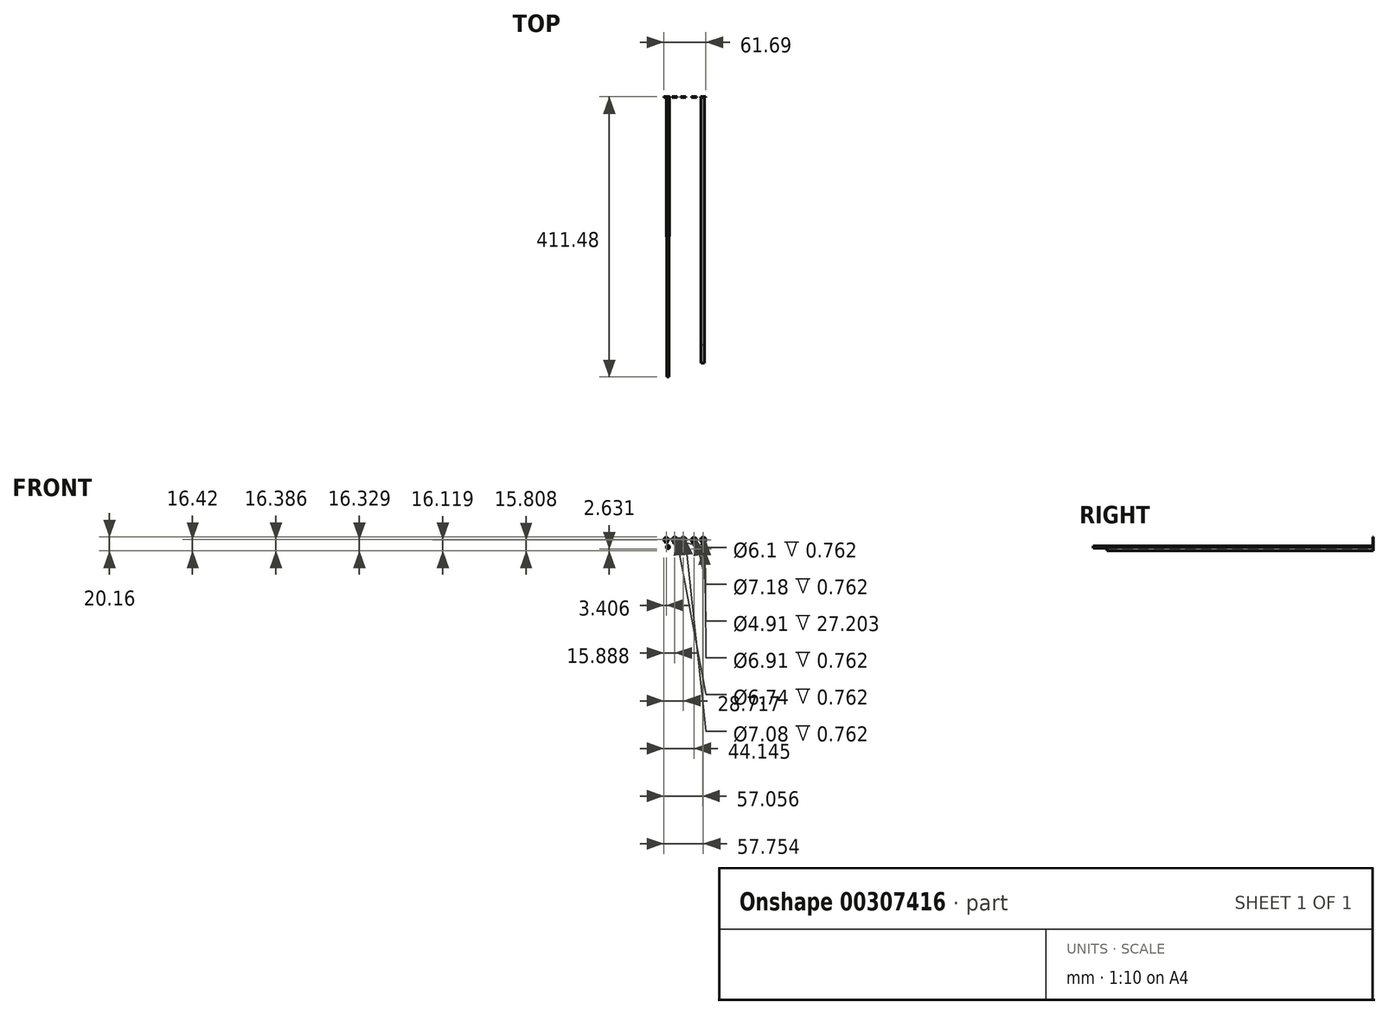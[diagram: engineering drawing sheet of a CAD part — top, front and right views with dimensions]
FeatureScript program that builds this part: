
annotation { "Feature Type Name" : "Feature", "Feature Type Description" : "" }
export const myFeature = defineFeature(function(context is Context, id is Id, definition is map)
    precondition{}
    {
        {
            var Q0;
            Q0=qCreatedBy(makeId("Front.planeOp"),FACE);
            var sketch = newSketch(context, id + "F0", { "sketchPlane" : qUnion([Q0])});
            skCircle(sketch, "E0", {"center": v(33.39, 22.16) * mm, "radius": 2.63 * mm});
            skSolve(sketch);
        }
        {
            var Q0;
            Q0=makeQuery(id+"F0.imprint","IMPRINT",FACE,{"disambiguationData":[TD([[makeQuery(id+"F0.imprint","IMPRINT",EDGE,{"derivedFrom":sQuery(id+"F0.wireOp",EDGE,"E0")}),1.0]])]});
            extrude(context, id + "F1", {"entities" : qUnion([Q0]), "depth" : 391.16 * mm});
        }
        {
            var Q0;
            Q0=makeQuery(id+"F1.opExtrude","CAP_FACE",FACE,{"disambiguationData":[OSD([sQuery(id+"F0.wireOp",EDGE,"E0")])],"isStart":false});
            var sketch = newSketch(context, id + "F2", { "sketchPlane" : qUnion([Q0])});
            skCircle(sketch, "E1", {"center": v(33.39, 22.16) * mm, "radius": 2.45 * mm});
            skSolve(sketch);
        }
        {
            var Q0;
            Q0 = qSketchRegion(id + "F2", true);
            extrude(context, id + "F3", {"entities" : qUnion([Q0]), "operationType" : NewBodyOperationType.REMOVE, "oppositeDirection" : true, "depth" : 27.2 * mm});
        }
        {
            var Q0;
            Q0=qCreatedBy(makeId("Front.planeOp"),FACE);
            var sketch = newSketch(context, id + "F4", { "sketchPlane" : qUnion([Q0])});
            skCircle(sketch, "E2", {"center": v(-17.76, 24.97) * mm, "radius": 2.45 * mm});
            skSolve(sketch);
        }
        {
            var Q0;
            Q0=makeQuery(id+"F4.imprint","IMPRINT",FACE,{"disambiguationData":[TD([[makeQuery(id+"F4.imprint","IMPRINT",EDGE,{"derivedFrom":sQuery(id+"F4.wireOp",EDGE,"E2")}),1.0]])]});
            extrude(context, id + "F5", {"entities" : qUnion([Q0]), "depth" : 411.48 * mm, "hasDraft" : true, "draftAngle" : 0.1 * degree, "draftPullDirection" : true});
        }
        {
            var Q0;
            Q0=qCreatedBy(makeId("Front.planeOp"),FACE);
            var sketch = newSketch(context, id + "F6", { "sketchPlane" : qUnion([Q0])});
            skCircle(sketch, "E3", {"center": v(34.08, 35.65) * mm, "radius": 3.93 * mm});
            skCircle(sketch, "E4", {"center": v(34.08, 35.65) * mm, "radius": 3.46 * mm});
            skLineSegment(sketch, "E5", {"start": v(34.31, 31.72) * mm, "end": v(34.31, 28.21) * mm});
            skLineSegment(sketch, "E6", {"start": v(33.85, 31.72) * mm, "end": v(33.85, 28.21) * mm});
            skLineSegment(sketch, "E7", {"start": v(33.85, 28.21) * mm, "end": v(34.31, 28.21) * mm});
            skLineSegment(sketch, "E8", {"start": v(35.77, 32.1) * mm, "end": v(36.19, 28.21) * mm});
            skLineSegment(sketch, "E9", {"start": v(36.19, 28.21) * mm, "end": v(35.55, 28.21) * mm});
            skLineSegment(sketch, "E10", {"start": v(35.55, 28.21) * mm, "end": v(35.3, 31.91) * mm});
            skLineSegment(sketch, "E11", {"start": v(32.4, 32.1) * mm, "end": v(32.14, 28.21) * mm});
            skLineSegment(sketch, "E12", {"start": v(32.14, 28.21) * mm, "end": v(32.68, 28.18) * mm});
            skLineSegment(sketch, "E13", {"start": v(32.68, 28.18) * mm, "end": v(32.92, 31.91) * mm});
            skSolve(sketch);
        }
        {
            var Q0;
            Q0=makeQuery(id+"F6.imprint","IMPRINT",FACE,{"disambiguationData":[TD([[makeQuery(id+"F6.imprint","IMPRINT",EDGE,{"derivedFrom":sQuery(id+"F6.wireOp",EDGE,"E4")}),-1.0]])]});
            var Q1;
            {var subQ0=sQuery(id+"F6.wireOp",EDGE,"AtMkA9jw-oHao-wLgf-iVHr-EhoPNY91XVLY");Q1=makeQuery(id+"F6.imprint","IMPRINT",FACE,{"disambiguationData":[TD([[makeQuery(id+"F6.imprint","IMPRINT",EDGE,{"derivedFrom":subQ0}),-1.0]])]});}
            var Q2;
            {var subQ0=sQuery(id+"F6.wireOp",EDGE,"G1UfZidr-wi69-PWyG-ggrf-osr7YpHfYW1K");Q2=makeQuery(id+"F6.imprint","IMPRINT",FACE,{"disambiguationData":[TD([[makeQuery(id+"F6.imprint","IMPRINT",EDGE,{"derivedFrom":subQ0}),1.0]])]});}
            var Q3;
            {var subQ0=sQuery(id+"F6.wireOp",EDGE,"wkRRPSaf-uJ6Z-lWe9-TKJw-fEsDiBzZJhiO");Q3=makeQuery(id+"F6.imprint","IMPRINT",FACE,{"disambiguationData":[TD([[makeQuery(id+"F6.imprint","IMPRINT",EDGE,{"derivedFrom":subQ0}),1.0]])]});}
            extrude(context, id + "F7", {"entities" : qUnion([Q0, Q1, Q2, Q3]), "depth" : 0.76 * mm});
        }
        {
            var Q0;
            Q0=makeQuery(id+"F6.imprint","IMPRINT",FACE,{"disambiguationData":[TD([[makeQuery(id+"F6.imprint","IMPRINT",EDGE,{"derivedFrom":sQuery(id+"F6.wireOp",EDGE,"E4")}),-1.0]])]});
            var Q1;
            {var subQ0=sQuery(id+"F6.wireOp",EDGE,"E11");Q1=makeQuery(id+"F6.imprint","IMPRINT",FACE,{"disambiguationData":[TD([[makeQuery(id+"F6.imprint","IMPRINT",EDGE,{"derivedFrom":subQ0}),1.0]])]});}
            var Q2;
            {var subQ0=sQuery(id+"F6.wireOp",EDGE,"E5");Q2=makeQuery(id+"F6.imprint","IMPRINT",FACE,{"disambiguationData":[TD([[makeQuery(id+"F6.imprint","IMPRINT",EDGE,{"derivedFrom":subQ0}),-1.0]])]});}
            var Q3;
            {var subQ0=sQuery(id+"F6.wireOp",EDGE,"E8");Q3=makeQuery(id+"F6.imprint","IMPRINT",FACE,{"disambiguationData":[TD([[makeQuery(id+"F6.imprint","IMPRINT",EDGE,{"derivedFrom":subQ0}),-1.0]])]});}
            extrude(context, id + "F8", {"entities" : qUnion([Q0, Q1, Q2, Q3]), "operationType" : NewBodyOperationType.ADD, "depth" : 0.76 * mm});
        }
        {
            var Q0;
            Q0=qCreatedBy(makeId("Front.planeOp"),FACE);
            var sketch = newSketch(context, id + "F9", { "sketchPlane" : qUnion([Q0])});
            skCircle(sketch, "E14", {"center": v(20.47, 35.34) * mm, "radius": 3.86 * mm});
            skCircle(sketch, "E15", {"center": v(20.47, 35.34) * mm, "radius": 3.59 * mm});
            skLineSegment(sketch, "E16", {"start": v(20.63, 31.48) * mm, "end": v(20.63, 28.75) * mm});
            skLineSegment(sketch, "E17", {"start": v(20.63, 28.75) * mm, "end": v(20.17, 28.75) * mm});
            skLineSegment(sketch, "E18", {"start": v(20.17, 28.75) * mm, "end": v(20.17, 31.48) * mm});
            skLineSegment(sketch, "E19", {"start": v(22.13, 31.85) * mm, "end": v(22.27, 28.75) * mm});
            skLineSegment(sketch, "E20", {"start": v(22.27, 28.75) * mm, "end": v(21.87, 28.74) * mm});
            skLineSegment(sketch, "E21", {"start": v(21.87, 28.74) * mm, "end": v(21.74, 31.68) * mm});
            skLineSegment(sketch, "E22", {"start": v(18.82, 31.85) * mm, "end": v(18.7, 28.75) * mm});
            skLineSegment(sketch, "E23", {"start": v(18.7, 28.75) * mm, "end": v(19.17, 28.74) * mm});
            skLineSegment(sketch, "E24", {"start": v(19.17, 28.74) * mm, "end": v(19.28, 31.68) * mm});
            skSolve(sketch);
        }
        {
            var Q0;
            Q0=makeQuery(id+"F9.imprint","IMPRINT",FACE,{"disambiguationData":[TD([[makeQuery(id+"F9.imprint","IMPRINT",EDGE,{"derivedFrom":sQuery(id+"F9.wireOp",EDGE,"E15")}),-1.0]])]});
            var Q1;
            {var subQ0=sQuery(id+"F9.wireOp",EDGE,"E19");Q1=makeQuery(id+"F9.imprint","IMPRINT",FACE,{"disambiguationData":[TD([[makeQuery(id+"F9.imprint","IMPRINT",EDGE,{"derivedFrom":subQ0}),-1.0]])]});}
            var Q2;
            {var subQ0=sQuery(id+"F9.wireOp",EDGE,"E16");Q2=makeQuery(id+"F9.imprint","IMPRINT",FACE,{"disambiguationData":[TD([[makeQuery(id+"F9.imprint","IMPRINT",EDGE,{"derivedFrom":subQ0}),-1.0]])]});}
            var Q3;
            {var subQ0=sQuery(id+"F9.wireOp",EDGE,"E22");Q3=makeQuery(id+"F9.imprint","IMPRINT",FACE,{"disambiguationData":[TD([[makeQuery(id+"F9.imprint","IMPRINT",EDGE,{"derivedFrom":subQ0}),1.0]])]});}
            extrude(context, id + "F10", {"entities" : qUnion([Q0, Q1, Q2, Q3]), "depth" : 0.76 * mm});
        }
        {
            var Q0;
            Q0=qCreatedBy(makeId("Front.planeOp"),FACE);
            var sketch = newSketch(context, id + "F11", { "sketchPlane" : qUnion([Q0])});
            skCircle(sketch, "E25", {"center": v(5.05, 35.86) * mm, "radius": 3.83 * mm});
            skCircle(sketch, "E26", {"center": v(5.05, 35.86) * mm, "radius": 3.54 * mm});
            skLineSegment(sketch, "E27", {"start": v(5.28, 32.04) * mm, "end": v(5.28, 29.42) * mm});
            skLineSegment(sketch, "E28", {"start": v(5.28, 29.42) * mm, "end": v(4.85, 29.42) * mm});
            skLineSegment(sketch, "E29", {"start": v(4.85, 29.42) * mm, "end": v(4.85, 32.03) * mm});
            skLineSegment(sketch, "E30", {"start": v(6.44, 32.3) * mm, "end": v(6.65, 29.42) * mm});
            skLineSegment(sketch, "E31", {"start": v(6.65, 29.42) * mm, "end": v(6.27, 29.4) * mm});
            skLineSegment(sketch, "E32", {"start": v(6.27, 29.4) * mm, "end": v(6.06, 32.17) * mm});
            skLineSegment(sketch, "E33", {"start": v(3.66, 32.3) * mm, "end": v(3.58, 29.42) * mm});
            skLineSegment(sketch, "E34", {"start": v(3.58, 29.42) * mm, "end": v(3.92, 29.42) * mm});
            skLineSegment(sketch, "E35", {"start": v(3.92, 29.42) * mm, "end": v(3.92, 32.2) * mm});
            skSolve(sketch);
        }
        {
            var Q0;
            Q0=makeQuery(id+"F11.imprint","IMPRINT",FACE,{"disambiguationData":[TD([[makeQuery(id+"F11.imprint","IMPRINT",EDGE,{"derivedFrom":sQuery(id+"F11.wireOp",EDGE,"E26")}),-1.0]])]});
            var Q1;
            {var subQ0=sQuery(id+"F11.wireOp",EDGE,"E27");Q1=makeQuery(id+"F11.imprint","IMPRINT",FACE,{"disambiguationData":[TD([[makeQuery(id+"F11.imprint","IMPRINT",EDGE,{"derivedFrom":subQ0}),-1.0]])]});}
            var Q2;
            {var subQ0=sQuery(id+"F11.wireOp",EDGE,"E33");Q2=makeQuery(id+"F11.imprint","IMPRINT",FACE,{"disambiguationData":[TD([[makeQuery(id+"F11.imprint","IMPRINT",EDGE,{"derivedFrom":subQ0}),1.0]])]});}
            var Q3;
            {var subQ0=sQuery(id+"F11.wireOp",EDGE,"E30");Q3=makeQuery(id+"F11.imprint","IMPRINT",FACE,{"disambiguationData":[TD([[makeQuery(id+"F11.imprint","IMPRINT",EDGE,{"derivedFrom":subQ0}),-1.0]])]});}
            extrude(context, id + "F12", {"entities" : qUnion([Q0, Q1, Q2, Q3]), "depth" : 0.76 * mm});
        }
        {
            var Q0;
            Q0=qCreatedBy(makeId("Front.planeOp"),FACE);
            var sketch = newSketch(context, id + "F13", { "sketchPlane" : qUnion([Q0])});
            skCircle(sketch, "E36", {"center": v(-7.78, 35.95) * mm, "radius": 3.68 * mm});
            skCircle(sketch, "E37", {"center": v(-7.78, 35.95) * mm, "radius": 3.37 * mm});
            skLineSegment(sketch, "E38", {"start": v(-7.48, 32.29) * mm, "end": v(-7.48, 29.73) * mm});
            skLineSegment(sketch, "E39", {"start": v(-7.48, 29.73) * mm, "end": v(-7.92, 29.73) * mm});
            skLineSegment(sketch, "E40", {"start": v(-7.92, 29.73) * mm, "end": v(-7.92, 32.28) * mm});
            skLineSegment(sketch, "E41", {"start": v(-6.5, 32.5) * mm, "end": v(-6.3, 29.75) * mm});
            skLineSegment(sketch, "E42", {"start": v(-6.3, 29.75) * mm, "end": v(-6.64, 29.73) * mm});
            skLineSegment(sketch, "E43", {"start": v(-6.64, 29.73) * mm, "end": v(-6.83, 32.4) * mm});
            skLineSegment(sketch, "E44", {"start": v(-9.06, 32.5) * mm, "end": v(-9.18, 29.73) * mm});
            skLineSegment(sketch, "E45", {"start": v(-9.18, 29.73) * mm, "end": v(-8.79, 29.7) * mm});
            skLineSegment(sketch, "E46", {"start": v(-8.79, 29.7) * mm, "end": v(-8.67, 32.38) * mm});
            skSolve(sketch);
        }
        {
            var Q0;
            Q0=makeQuery(id+"F13.imprint","IMPRINT",FACE,{"disambiguationData":[TD([[makeQuery(id+"F13.imprint","IMPRINT",EDGE,{"derivedFrom":sQuery(id+"F13.wireOp",EDGE,"E37")}),-1.0]])]});
            var Q1;
            {var subQ0=sQuery(id+"F13.wireOp",EDGE,"E38");Q1=makeQuery(id+"F13.imprint","IMPRINT",FACE,{"disambiguationData":[TD([[makeQuery(id+"F13.imprint","IMPRINT",EDGE,{"derivedFrom":subQ0}),-1.0]])]});}
            var Q2;
            {var subQ0=sQuery(id+"F13.wireOp",EDGE,"E44");Q2=makeQuery(id+"F13.imprint","IMPRINT",FACE,{"disambiguationData":[TD([[makeQuery(id+"F13.imprint","IMPRINT",EDGE,{"derivedFrom":subQ0}),1.0]])]});}
            var Q3;
            {var subQ0=sQuery(id+"F13.wireOp",EDGE,"E41");Q3=makeQuery(id+"F13.imprint","IMPRINT",FACE,{"disambiguationData":[TD([[makeQuery(id+"F13.imprint","IMPRINT",EDGE,{"derivedFrom":subQ0}),-1.0]])]});}
            extrude(context, id + "F14", {"entities" : qUnion([Q0, Q1, Q2, Q3]), "depth" : 0.76 * mm});
        }
        {
            var Q0;
            Q0=qCreatedBy(makeId("Front.planeOp"),FACE);
            var sketch = newSketch(context, id + "F15", { "sketchPlane" : qUnion([Q0])});
            skCircle(sketch, "E47", {"center": v(-20.26, 35.92) * mm, "radius": 3.4 * mm});
            skCircle(sketch, "E48", {"center": v(-20.26, 35.92) * mm, "radius": 3.05 * mm});
            skLineSegment(sketch, "E49", {"start": v(-20.05, 32.52) * mm, "end": v(-20.05, 30.62) * mm});
            skLineSegment(sketch, "E50", {"start": v(-20.05, 30.62) * mm, "end": v(-20.31, 30.62) * mm});
            skLineSegment(sketch, "E51", {"start": v(-20.31, 30.62) * mm, "end": v(-20.31, 32.51) * mm});
            skLineSegment(sketch, "E52", {"start": v(-19.1, 32.72) * mm, "end": v(-19.01, 30.62) * mm});
            skLineSegment(sketch, "E53", {"start": v(-19.01, 30.62) * mm, "end": v(-19.25, 30.61) * mm});
            skLineSegment(sketch, "E54", {"start": v(-19.25, 30.61) * mm, "end": v(-19.33, 32.64) * mm});
            skLineSegment(sketch, "E55", {"start": v(-21.43, 32.72) * mm, "end": v(-21.5, 30.7) * mm});
            skLineSegment(sketch, "E56", {"start": v(-21.5, 30.7) * mm, "end": v(-21.26, 30.7) * mm});
            skLineSegment(sketch, "E57", {"start": v(-21.26, 30.7) * mm, "end": v(-21.2, 32.64) * mm});
            skSolve(sketch);
        }
        {
            var Q0;
            Q0=makeQuery(id+"F15.imprint","IMPRINT",FACE,{"disambiguationData":[TD([[makeQuery(id+"F15.imprint","IMPRINT",EDGE,{"derivedFrom":sQuery(id+"F15.wireOp",EDGE,"E48")}),-1.0]])]});
            var Q1;
            {var subQ0=sQuery(id+"F15.wireOp",EDGE,"E49");Q1=makeQuery(id+"F15.imprint","IMPRINT",FACE,{"disambiguationData":[TD([[makeQuery(id+"F15.imprint","IMPRINT",EDGE,{"derivedFrom":subQ0}),-1.0]])]});}
            var Q2;
            {var subQ0=sQuery(id+"F15.wireOp",EDGE,"E55");Q2=makeQuery(id+"F15.imprint","IMPRINT",FACE,{"disambiguationData":[TD([[makeQuery(id+"F15.imprint","IMPRINT",EDGE,{"derivedFrom":subQ0}),1.0]])]});}
            var Q3;
            {var subQ0=sQuery(id+"F15.wireOp",EDGE,"E52");Q3=makeQuery(id+"F15.imprint","IMPRINT",FACE,{"disambiguationData":[TD([[makeQuery(id+"F15.imprint","IMPRINT",EDGE,{"derivedFrom":subQ0}),-1.0]])]});}
            extrude(context, id + "F16", {"entities" : qUnion([Q0, Q1, Q2, Q3]), "depth" : 0.76 * mm});
        }
    });
